annotation { "Feature Type Name" : "Feature", "Feature Type Description" : "" }
export const myFeature = defineFeature(function(context is Context, id is Id, definition is map)
    precondition{}
    {
        {
            var Q0;
            Q0=qCreatedBy(makeId("Front.planeOp"),FACE);
            var sketch = newSketch(context, id + "F0", { "sketchPlane" : qUnion([Q0])});
            skLineSegment(sketch, "E0.bottom", {"start": v(0, 0) * mm, "end": v(-300, 0) * mm, "construction": true});
            skLineSegment(sketch, "E0.top", {"start": v(0, -200) * mm, "end": v(-300, -200) * mm, "construction": true});
            skLineSegment(sketch, "E0.left", {"start": v(0, 0) * mm, "end": v(0, -200) * mm, "construction": true});
            skLineSegment(sketch, "E0.right", {"start": v(-300, 0) * mm, "end": v(-300, -200) * mm, "construction": true});
            skLineSegment(sketch, "E1", {"start": v(-300, -142.29) * mm, "end": v(0, -142.29) * mm});
            skArc(sketch, "E2", {"start": v(-23.68, -200) * mm, "mid": v(-6.6, -197.75) * mm, "end": v(0, -181.82) * mm});
            skArc(sketch, "E3", {"start": v(-300, -182.35) * mm, "mid": v(-295.32, -196.6) * mm, "end": v(-280.71, -200) * mm});
            skText(sketch, "E4", { "text": "SAN FRANCISCO", "fontName": "OpenSans-Regular.ttf"});
            skLineSegment(sketch, "E5", {"start": v(-286.41, -142.29) * mm, "end": v(-149.86, -74) * mm});
            skLineSegment(sketch, "E6", {"start": v(-300, -118.66) * mm, "end": v(-169, -58.68) * mm});
            skLineSegment(sketch, "E7", {"start": v(-242.93, -120.54) * mm, "end": v(-242.93, -142.29) * mm});
            skLineSegment(sketch, "E8", {"start": v(-250.93, -124.54) * mm, "end": v(-250.93, -142.29) * mm});
            skLineSegment(sketch, "E9", {"start": v(-238.34, -118.25) * mm, "end": v(-238.34, -142.29) * mm});
            skLineSegment(sketch, "E10", {"start": v(-254.5, -126.33) * mm, "end": v(-254.5, -142.29) * mm});
            skLineSegment(sketch, "E11", {"start": v(-242.93, -120.54) * mm, "end": v(-242.93, -92.53) * mm});
            skLineSegment(sketch, "E12", {"start": v(-238.34, -118.25) * mm, "end": v(-238.34, -90.43) * mm});
            skLineSegment(sketch, "E13", {"start": v(-258.9, -99.84) * mm, "end": v(-258.9, -68.69) * mm});
            skLineSegment(sketch, "E14", {"start": v(-258.9, -68.69) * mm, "end": v(-237.27, -68.69) * mm});
            skLineSegment(sketch, "E15", {"start": v(-237.27, -89.94) * mm, "end": v(-242.93, -92.53) * mm});
            skLineSegment(sketch, "E16", {"start": v(-242.93, -74.88) * mm, "end": v(-253.53, -74.88) * mm});
            skLineSegment(sketch, "E17", {"start": v(-253.53, -74.88) * mm, "end": v(-253.53, -97.38) * mm});
            skLineSegment(sketch, "E18", {"start": v(-253.53, -97.38) * mm, "end": v(-242.93, -92.53) * mm});
            skLineSegment(sketch, "E19", {"start": v(-242.93, -92.53) * mm, "end": v(-242.93, -74.88) * mm});
            skLineSegment(sketch, "E20", {"start": v(-242.93, -68.69) * mm, "end": v(-239.93, -68.69) * mm});
            skLineSegment(sketch, "E21", {"start": v(-239.93, -68.69) * mm, "end": v(-239.93, -43.85) * mm});
            skLineSegment(sketch, "E22", {"start": v(-239.93, -43.85) * mm, "end": v(-255.87, -43.85) * mm});
            skLineSegment(sketch, "E23", {"start": v(-255.87, -43.85) * mm, "end": v(-255.87, -68.69) * mm});
            skLineSegment(sketch, "E24", {"start": v(-255.87, -68.69) * mm, "end": v(-251.7, -68.69) * mm});
            skLineSegment(sketch, "E25", {"start": v(-251.7, -68.69) * mm, "end": v(-251.7, -47.78) * mm});
            skLineSegment(sketch, "E26", {"start": v(-251.7, -47.78) * mm, "end": v(-245.15, -47.78) * mm});
            skLineSegment(sketch, "E27", {"start": v(-245.15, -47.78) * mm, "end": v(-245.15, -68.69) * mm});
            skLineSegment(sketch, "E28", {"start": v(-245.15, -68.69) * mm, "end": v(-245.15, -47.78) * mm});
            skLineSegment(sketch, "E29", {"start": v(-253.53, -43.85) * mm, "end": v(-253.53, -23.5) * mm});
            skLineSegment(sketch, "E30", {"start": v(-253.53, -23.5) * mm, "end": v(-242.93, -23.5) * mm});
            skLineSegment(sketch, "E31", {"start": v(-242.93, -23.5) * mm, "end": v(-242.93, -43.85) * mm});
            skLineSegment(sketch, "E32", {"start": v(-242.93, -43.85) * mm, "end": v(-245.15, -43.85) * mm});
            skLineSegment(sketch, "E33", {"start": v(-245.8, -43.85) * mm, "end": v(-245.8, -26.41) * mm});
            skLineSegment(sketch, "E34", {"start": v(-245.8, -26.41) * mm, "end": v(-245.8, -43.85) * mm});
            skLineSegment(sketch, "E35", {"start": v(-251.22, -43.85) * mm, "end": v(-251.22, -26.41) * mm});
            skLineSegment(sketch, "E36", {"start": v(-251.22, -26.41) * mm, "end": v(-245.8, -26.41) * mm});
            skLineSegment(sketch, "E37", {"start": v(-249.88, -23.5) * mm, "end": v(-249.88, -18.66) * mm});
            skLineSegment(sketch, "E38", {"start": v(-249.88, -18.66) * mm, "end": v(-247.02, -18.66) * mm});
            skLineSegment(sketch, "E39", {"start": v(-247.02, -18.66) * mm, "end": v(-247.02, -23.5) * mm});
            skLineSegment(sketch, "E40", {"start": v(-247.02, -23.5) * mm, "end": v(-245.8, -23.5) * mm});
            skLineSegment(sketch, "E41", {"start": v(-245.8, -23.5) * mm, "end": v(-245.8, -16.65) * mm});
            skLineSegment(sketch, "E42", {"start": v(-245.8, -16.65) * mm, "end": v(-251.22, -16.65) * mm});
            skLineSegment(sketch, "E43", {"start": v(-251.22, -16.65) * mm, "end": v(-251.22, -23.5) * mm});
            skLineSegment(sketch, "E44", {"start": v(-251.22, -23.5) * mm, "end": v(-251.22, -16.65) * mm});
            skLineSegment(sketch, "E45", {"start": v(-251.22, -16.65) * mm, "end": v(-251.22, -15.7) * mm});
            skLineSegment(sketch, "E46", {"start": v(-251.22, -15.7) * mm, "end": v(-250.58, -15.7) * mm});
            skLineSegment(sketch, "E47", {"start": v(-250.58, -15.7) * mm, "end": v(-250.58, -16.65) * mm});
            skLineSegment(sketch, "E48", {"start": v(-250.58, -16.65) * mm, "end": v(-250.58, -15.78) * mm});
            skLineSegment(sketch, "E49", {"start": v(-250.58, -15.78) * mm, "end": v(-250.58, -15.7) * mm});
            skLineSegment(sketch, "E50", {"start": v(-251.02, -15.7) * mm, "end": v(-251.02, -15.4) * mm});
            skLineSegment(sketch, "E51", {"start": v(-250.78, -15.7) * mm, "end": v(-250.78, -15.4) * mm});
            skLineSegment(sketch, "E52", {"start": v(-250.78, -15.4) * mm, "end": v(-251, -15.4) * mm});
            skLineSegment(sketch, "E53", {"start": v(-245.8, -16.65) * mm, "end": v(-245.8, -15.8) * mm});
            skLineSegment(sketch, "E54", {"start": v(-245.8, -15.8) * mm, "end": v(-246.36, -15.8) * mm});
            skLineSegment(sketch, "E55", {"start": v(-246.36, -15.8) * mm, "end": v(-246.36, -16.65) * mm});
            skLineSegment(sketch, "E56", {"start": v(-246.36, -16.65) * mm, "end": v(-246.36, -15.8) * mm});
            skLineSegment(sketch, "E57", {"start": v(-246.17, -15.8) * mm, "end": v(-246.17, -15.5) * mm});
            skLineSegment(sketch, "E58", {"start": v(-246.17, -15.5) * mm, "end": v(-245.95, -15.5) * mm});
            skLineSegment(sketch, "E59", {"start": v(-245.95, -15.5) * mm, "end": v(-245.95, -15.8) * mm});
            skLineSegment(sketch, "E60", {"start": v(-238.34, -90.43) * mm, "end": v(-238.34, -68.69) * mm});
            skLineSegment(sketch, "E61", {"start": v(-116.56, -142.29) * mm, "end": v(-131.45, -142.29) * mm});
            skLineSegment(sketch, "E62", {"start": v(-149.86, -74) * mm, "end": v(-91.02, -44.57) * mm});
            skLineSegment(sketch, "E63", {"start": v(-169, -58.68) * mm, "end": v(-94.48, -23.38) * mm});
            skLineSegment(sketch, "E64", {"start": v(-91.02, -44.57) * mm, "end": v(-91.02, -60.73) * mm});
            skLineSegment(sketch, "E65", {"start": v(-91.02, -60.73) * mm, "end": v(-81.78, -60.73) * mm});
            skLineSegment(sketch, "E66", {"start": v(-81.78, -60.73) * mm, "end": v(-81.78, -5.29) * mm});
            skLineSegment(sketch, "E67", {"start": v(-81.78, -5.29) * mm, "end": v(-91.02, -5.29) * mm});
            skLineSegment(sketch, "E68", {"start": v(-91.02, -5.29) * mm, "end": v(-91.02, -44.57) * mm});
            skLineSegment(sketch, "E69", {"start": v(-94.48, -23.38) * mm, "end": v(-91.02, -21.65) * mm});
            skPoint(sketch, "E69.endSnap0", {"position": v(-91.02, -24.93) * mm});
            skLineSegment(sketch, "E70", {"start": v(-91.02, -44.57) * mm, "end": v(-81.78, -40.19) * mm});
            skLineSegment(sketch, "E71", {"start": v(-91.02, -13.76) * mm, "end": v(-81.78, -13.76) * mm});
            skLineSegment(sketch, "E72", {"start": v(-91.02, -21.65) * mm, "end": v(-81.78, -21.65) * mm});
            skLineSegment(sketch, "E73", {"start": v(-81.78, -21.65) * mm, "end": v(-81.78, -29.93) * mm});
            skLineSegment(sketch, "E74", {"start": v(-81.78, -29.93) * mm, "end": v(-91.02, -29.93) * mm});
            skLineSegment(sketch, "E75", {"start": v(-91.02, -29.93) * mm, "end": v(-91.02, -44.57) * mm});
            skLineSegment(sketch, "E76", {"start": v(-91.02, -44.57) * mm, "end": v(-81.78, -44.57) * mm});
            skArc(sketch, "E77", {"start": v(-245.8, -15.8) * mm, "mid": v(-161.83, -41.2) * mm, "end": v(-81.78, -5.29) * mm});
            skArc(sketch, "E78", {"start": v(-250.58, -15.7) * mm, "mid": v(-168.33, -48.35) * mm, "end": v(-91.02, -5.29) * mm});
            skLineSegment(sketch, "E79", {"start": v(-100.7, -60.73) * mm, "end": v(-91.02, -60.73) * mm});
            skLineSegment(sketch, "E80", {"start": v(-81.78, -60.73) * mm, "end": v(0, -60.73) * mm});
            skLineSegment(sketch, "E81", {"start": v(0, -60.73) * mm, "end": v(0, -11.44) * mm});
            skLineSegment(sketch, "E82", {"start": v(0, -11.44) * mm, "end": v(-8.53, -11.44) * mm});
            skLineSegment(sketch, "E83", {"start": v(-8.53, -11.44) * mm, "end": v(-8.53, -5.07) * mm});
            skLineSegment(sketch, "E84", {"start": v(-8.53, -5.07) * mm, "end": v(-16.18, -5.07) * mm});
            skLineSegment(sketch, "E85", {"start": v(-16.18, -5.07) * mm, "end": v(-16.18, -25.89) * mm});
            skLineSegment(sketch, "E86", {"start": v(-16.18, -25.89) * mm, "end": v(-28.07, -25.89) * mm});
            skLineSegment(sketch, "E87", {"start": v(-28.07, -25.89) * mm, "end": v(-28.07, -19.51) * mm});
            skLineSegment(sketch, "E88", {"start": v(-28.07, -19.51) * mm, "end": v(-34.87, -19.51) * mm});
            skLineSegment(sketch, "E89", {"start": v(-34.87, -19.51) * mm, "end": v(-34.87, -33.53) * mm});
            skLineSegment(sketch, "E90", {"start": v(-34.87, -33.53) * mm, "end": v(-43.8, -33.53) * mm});
            skLineSegment(sketch, "E91", {"start": v(-43.8, -33.53) * mm, "end": v(-43.8, 0) * mm});
            skLineSegment(sketch, "E92", {"start": v(-43.8, 0) * mm, "end": v(-57.38, 0) * mm});
            skLineSegment(sketch, "E93", {"start": v(-57.38, 0) * mm, "end": v(-57.38, -10.6) * mm});
            skLineSegment(sketch, "E94", {"start": v(-57.38, -10.6) * mm, "end": v(-65.88, -10.6) * mm});
            skLineSegment(sketch, "E95", {"start": v(-65.88, -10.6) * mm, "end": v(-65.88, -19.51) * mm});
            skLineSegment(sketch, "E96", {"start": v(-65.88, -19.51) * mm, "end": v(-73.95, -19.51) * mm});
            skLineSegment(sketch, "E97", {"start": v(-73.95, -19.51) * mm, "end": v(-73.95, -60.73) * mm});
            skLineSegment(sketch, "E98", {"start": v(-300, -118.66) * mm, "end": v(-300, -142.29) * mm});
            skLineSegment(sketch, "E99", {"start": v(-81.78, -57.03) * mm, "end": v(-73.95, -57.71) * mm});
            skLineSegment(sketch, "E100", {"start": v(-91.02, -52.65) * mm, "end": v(-101.13, -52.65) * mm});
            skLineSegment(sketch, "E101", {"start": v(-101.13, -52.65) * mm, "end": v(-100.7, -60.73) * mm});
            const initialGuessF0  = {"E4": [-0.3, -0.18827, 1, 0, 0.02846]};
            skSetInitialGuess(sketch, initialGuessF0);
            skSolve(sketch);
        }
        {
            var Q0;
            Q0 = qSketchRegion(id + "F0", true);
            extrude(context, id + "F1", {"entities" : qUnion([Q0]), "depth" : 25 * mm, "offsetDistance" : 25 * mm});
        }
    });